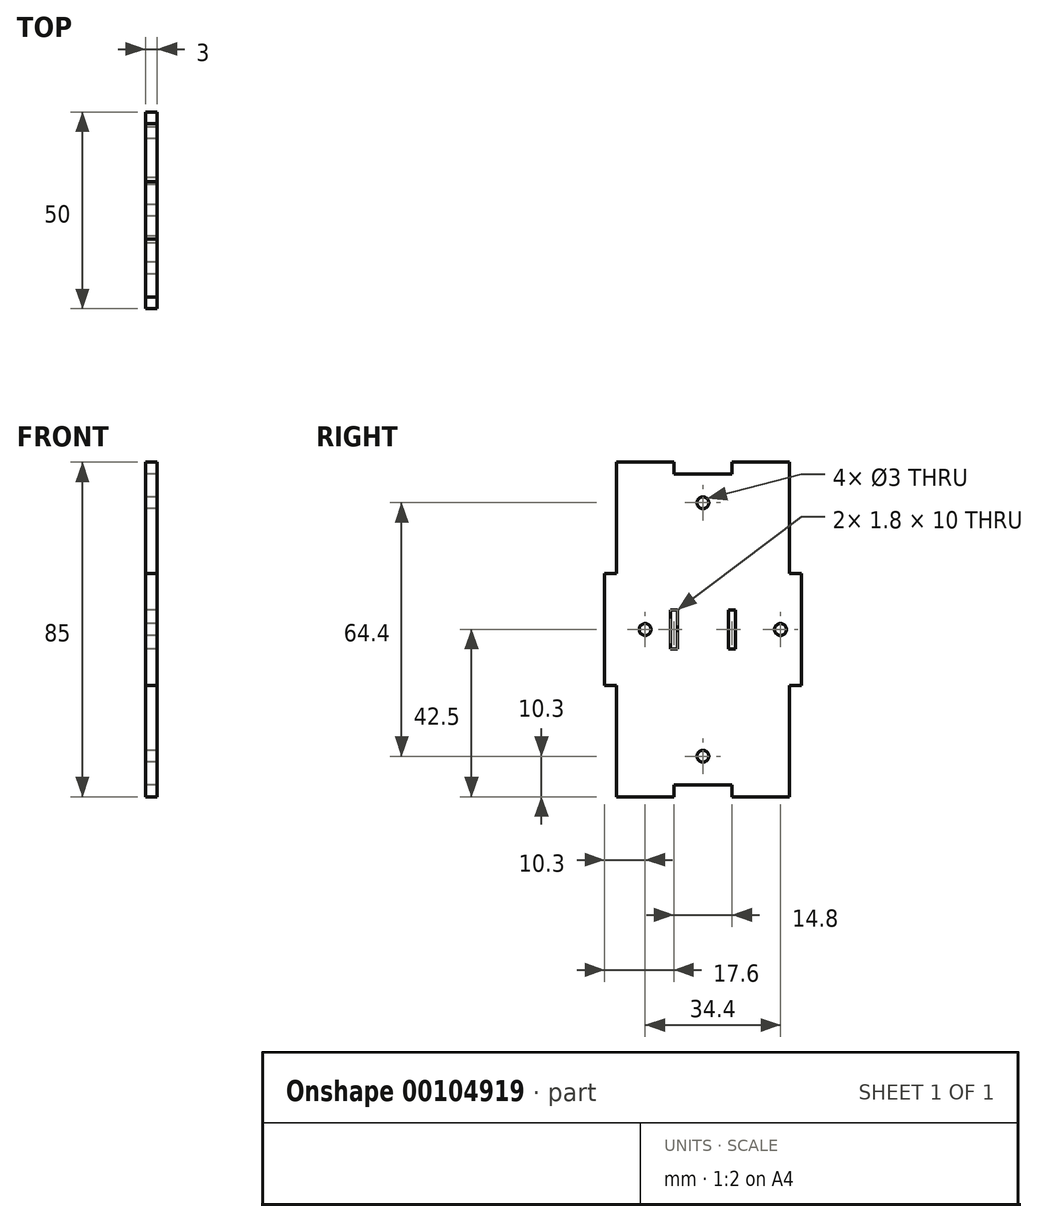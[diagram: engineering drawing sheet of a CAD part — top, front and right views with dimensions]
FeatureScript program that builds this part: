
annotation { "Feature Type Name" : "Feature", "Feature Type Description" : "" }
export const myFeature = defineFeature(function(context is Context, id is Id, definition is map)
    precondition{}
    {
        {
            var Q0;
            Q0=qCreatedBy(makeId("Right.planeOp"),FACE);
            var sketch = newSketch(context, id + "F0", { "sketchPlane" : qUnion([Q0])});
            skLineSegment(sketch, "E0.left", {"start": v(-25, 14.17) * mm, "end": v(-25, -14.17) * mm});
            skLineSegment(sketch, "E1.bottom", {"start": v(-25, 14.17) * mm, "end": v(-22, 14.17) * mm});
            skLineSegment(sketch, "E1.right", {"start": v(-22, 14.17) * mm, "end": v(-22, 42.5) * mm});
            skLineSegment(sketch, "E2.bottom", {"start": v(-25, -14.17) * mm, "end": v(-22, -14.17) * mm});
            skLineSegment(sketch, "E2.right", {"start": v(-22, -14.17) * mm, "end": v(-22, -42.5) * mm});
            skLineSegment(sketch, "E3.left", {"start": v(-7.33, 42.5) * mm, "end": v(-7.33, 39.5) * mm});
            skLineSegment(sketch, "E4.left", {"start": v(-7.33, -42.5) * mm, "end": v(-7.33, -39.5) * mm});
            skLineSegment(sketch, "E5", {"start": v(-7.33, 39.5) * mm, "end": v(0, 39.5) * mm});
            skLineSegment(sketch, "E6", {"start": v(0, 39.5) * mm, "end": v(0, 33.7) * mm});
            skLineSegment(sketch, "E7", {"start": v(0, -39.5) * mm, "end": v(-7.33, -39.5) * mm});
            skLineSegment(sketch, "E8", {"start": v(-22, 42.5) * mm, "end": v(-14.67, 42.5) * mm});
            skLineSegment(sketch, "E9", {"start": v(-14.67, 42.5) * mm, "end": v(-7.33, 42.5) * mm});
            skLineSegment(sketch, "E10", {"start": v(-7.33, -42.5) * mm, "end": v(-14.67, -42.5) * mm});
            skLineSegment(sketch, "E11", {"start": v(-14.67, -42.5) * mm, "end": v(-22, -42.5) * mm});
            skCircle(sketch, "E12", {"center": v(-14.7, 0) * mm, "radius": 1.5 * mm});
            skLineSegment(sketch, "E13.bottom", {"start": v(-8.3, 5) * mm, "end": v(-6.5, 5) * mm});
            skLineSegment(sketch, "E13.top", {"start": v(-8.3, -5) * mm, "end": v(-6.5, -5) * mm});
            skLineSegment(sketch, "E13.left", {"start": v(-8.3, 5) * mm, "end": v(-8.3, -5) * mm});
            skLineSegment(sketch, "E13.right", {"start": v(-6.5, 5) * mm, "end": v(-6.5, -5) * mm});
            skArc(sketch, "E14", {"start": v(0, 33.7) * mm, "mid": v(-1.5, 32.2) * mm, "end": v(0, 30.7) * mm});
            skArc(sketch, "E15.MirrorCS", {"start": v(0, -33.7) * mm, "mid": v(-1.5, -32.2) * mm, "end": v(0, -30.7) * mm});
            skLineSegment(sketch, "E16.trimOffspring", {"start": v(0, 30.7) * mm, "end": v(0, -30.7) * mm});
            skLineSegment(sketch, "E17.trimOffspring", {"start": v(0, -33.7) * mm, "end": v(0, -39.5) * mm});
            skArc(sketch, "E18.MirrorCS", {"start": v(0, 33.7) * mm, "mid": v(1.5, 32.2) * mm, "end": v(0, 30.7) * mm});
            skLineSegment(sketch, "E19.MirrorCS", {"start": v(8.3, 5) * mm, "end": v(6.5, 5) * mm});
            skArc(sketch, "E20.MirrorCS", {"start": v(0, -33.7) * mm, "mid": v(1.5, -32.2) * mm, "end": v(0, -30.7) * mm});
            skLineSegment(sketch, "E21.MirrorCS", {"start": v(25, 14.17) * mm, "end": v(22, 14.17) * mm});
            skLineSegment(sketch, "E22.MirrorCS", {"start": v(7.33, -42.5) * mm, "end": v(7.33, -39.5) * mm});
            skLineSegment(sketch, "E23.MirrorCS", {"start": v(7.33, -42.5) * mm, "end": v(14.67, -42.5) * mm});
            skLineSegment(sketch, "E24.MirrorCS", {"start": v(25, -14.17) * mm, "end": v(22, -14.17) * mm});
            skLineSegment(sketch, "E25.MirrorCS", {"start": v(8.3, -5) * mm, "end": v(6.5, -5) * mm});
            skLineSegment(sketch, "E26.MirrorCS", {"start": v(14.67, 42.5) * mm, "end": v(7.33, 42.5) * mm});
            skLineSegment(sketch, "E27.MirrorCS", {"start": v(7.33, 42.5) * mm, "end": v(7.33, 39.5) * mm});
            skLineSegment(sketch, "E28.MirrorCS", {"start": v(6.5, 5) * mm, "end": v(6.5, -5) * mm});
            skLineSegment(sketch, "E29.MirrorCS", {"start": v(7.33, 39.5) * mm, "end": v(0, 39.5) * mm});
            skCircle(sketch, "E30.MirrorC", {"center": v(19.7, 0) * mm, "radius": 1.5 * mm});
            skLineSegment(sketch, "E31.MirrorCS", {"start": v(25, 14.17) * mm, "end": v(25, -14.17) * mm});
            skLineSegment(sketch, "E32.MirrorCS", {"start": v(22, -14.17) * mm, "end": v(22, -42.5) * mm});
            skLineSegment(sketch, "E33.MirrorCS", {"start": v(8.3, 5) * mm, "end": v(8.3, -5) * mm});
            skLineSegment(sketch, "E34.MirrorCS", {"start": v(0, -39.5) * mm, "end": v(7.33, -39.5) * mm});
            skLineSegment(sketch, "E35.MirrorCS", {"start": v(22, 42.5) * mm, "end": v(14.67, 42.5) * mm});
            skLineSegment(sketch, "E36.MirrorCS", {"start": v(22, 14.17) * mm, "end": v(22, 42.5) * mm});
            skLineSegment(sketch, "E37.MirrorCS", {"start": v(14.67, -42.5) * mm, "end": v(22, -42.5) * mm});
            skSolve(sketch);
        }
        {
            var Q0;
            Q0=qSketchRegion(id+"F0",true);
            extrude(context, id + "F1", {"entities" : qUnion([Q0]), "depth" : 3 * mm});
        }
    });
